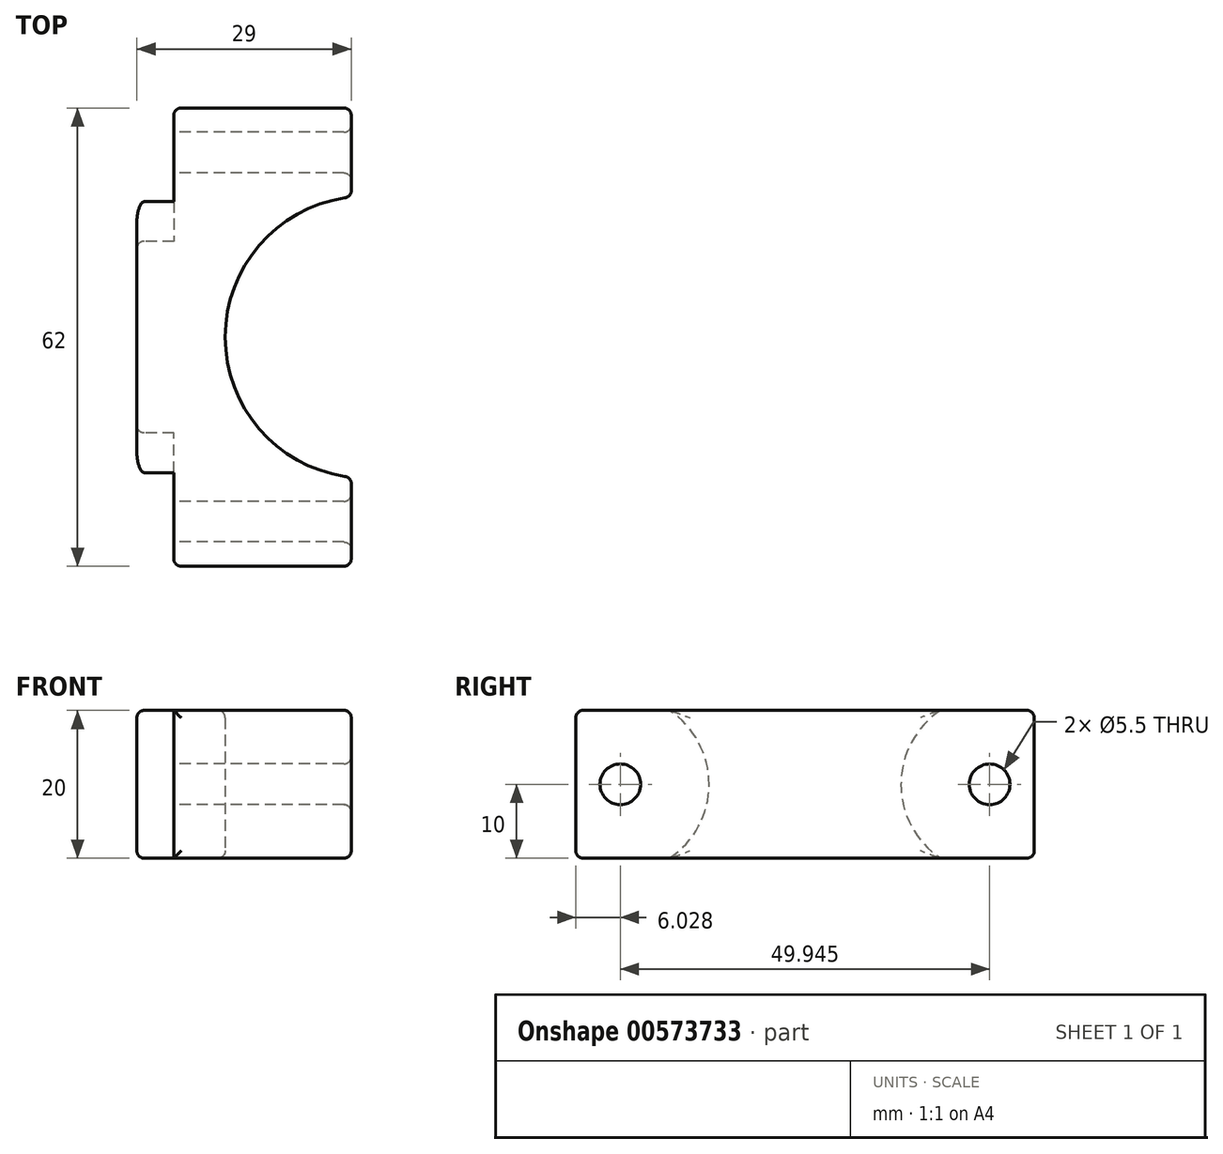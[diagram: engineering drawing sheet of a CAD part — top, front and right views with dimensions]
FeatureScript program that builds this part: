
annotation { "Feature Type Name" : "Feature", "Feature Type Description" : "" }
export const myFeature = defineFeature(function(context is Context, id is Id, definition is map)
    precondition{}
    {
        {
            var Q0;
            Q0=qCreatedBy(makeId("Top.planeOp"),FACE);
            var sketch = newSketch(context, id + "F0", { "sketchPlane" : qUnion([Q0])});
            skLineSegment(sketch, "E0.bottom", {"start": v(0, 0) * mm, "end": v(11.95, 0) * mm});
            skLineSegment(sketch, "E0.top", {"start": v(0, 31) * mm, "end": v(31, 31) * mm});
            skLineSegment(sketch, "E0.left", {"start": v(0, 0) * mm, "end": v(0, 31) * mm});
            skLineSegment(sketch, "E0.right", {"start": v(31, 19.05) * mm, "end": v(31, 31) * mm});
            skArc(sketch, "E1", {"start": v(31, 19.05) * mm, "mid": v(17.53, 13.47) * mm, "end": v(11.95, 0) * mm});
            skLineSegment(sketch, "E2.MirrorCS", {"start": v(0, 0) * mm, "end": v(0, -31) * mm});
            skLineSegment(sketch, "E3.MirrorCS", {"start": v(0, -31) * mm, "end": v(31, -31) * mm});
            skLineSegment(sketch, "E4.MirrorCS", {"start": v(31, -19.05) * mm, "end": v(31, -31) * mm});
            skArc(sketch, "E5.MirrorCS", {"start": v(31, -19.05) * mm, "mid": v(17.53, -13.47) * mm, "end": v(11.95, 0) * mm});
            skLineSegment(sketch, "E6", {"start": v(29, 31) * mm, "end": v(29, 18.94) * mm});
            skLineSegment(sketch, "E7.MirrorCS", {"start": v(29, -31) * mm, "end": v(29, -18.94) * mm});
            skSolve(sketch);
        }
        {
            var Q0;
            {var subQ0=sQuery(id+"F0.wireOp",EDGE,"E0.left");Q0=makeQuery(id+"F0.imprint","IMPRINT",FACE,{"disambiguationData":[TD([[makeQuery(id+"F0.imprint","IMPRINT",EDGE,{"derivedFrom":subQ0}),-1.0]])]});}
            var Q1;
            {var subQ4=sQuery(id+"F0.wireOp",EDGE,"E2.MirrorCS");Q1=makeQuery(id+"F0.imprint","IMPRINT",FACE,{"disambiguationData":[TD([[makeQuery(id+"F0.imprint","IMPRINT",EDGE,{"derivedFrom":subQ4}),1.0]])]});}
            extrude(context, id + "F1", {"entities" : qUnion([Q0, Q1]), "depth" : 20 * mm, "offsetDistance" : 25 * mm});
        }
        {
            var Q0;
            Q0=makeQuery(id+"F1.opExtrude","SWEPT_FACE",FACE,{"disambiguationData":[OSD([sQuery(id+"F0.wireOp",EDGE,"E0.left"),sQuery(id+"F0.wireOp",EDGE,"E2.MirrorCS")])]});
            var sketch = newSketch(context, id + "F2", { "sketchPlane" : qUnion([Q0])});
            skLineSegment(sketch, "E8.0.0", {"start": v(-18.94, 0) * mm, "end": v(-31, 0) * mm});
            skLineSegment(sketch, "E8.0.1", {"start": v(-31, 0) * mm, "end": v(-31, 20) * mm});
            skLineSegment(sketch, "E8.0.2", {"start": v(-31, 20) * mm, "end": v(-18.94, 20) * mm});
            skLineSegment(sketch, "E8.0.3", {"start": v(-18.94, 20) * mm, "end": v(-18.94, 0) * mm});
            skLineSegment(sketch, "E9", {"start": v(-24.97, 0) * mm, "end": v(-24.97, 20) * mm, "construction": true});
            skLineSegment(sketch, "E10", {"start": v(-31, 10) * mm, "end": v(-18.94, 10) * mm, "construction": true});
            skPoint(sketch, "E11", {"position": v(-24.97, 10) * mm});
            skPoint(sketch, "E12.MirrorP", {"position": v(24.97, 10) * mm});
            skSolve(sketch);
        }
        {
            var Q0;
            Q0=sQuery(id+"F2.wireOp",VERTEX,"E11");
            var Q1;
            Q1=sQuery(id+"F2.wireOp",VERTEX,"E12.MirrorP");
            var Q2;
            Q2=makeQuery(id+"F1.opExtrude","SWEPT_BODY",BODY,{"disambiguationData":[OSD([sQuery(id+"F0.wireOp",EDGE,"E0.top"),sQuery(id+"F0.wireOp",EDGE,"E0.left"),sQuery(id+"F0.wireOp",EDGE,"E0.right"),sQuery(id+"F0.wireOp",EDGE,"E1"),sQuery(id+"F0.wireOp",EDGE,"E2.MirrorCS"),sQuery(id+"F0.wireOp",EDGE,"E3.MirrorCS"),sQuery(id+"F0.wireOp",EDGE,"E4.MirrorCS"),sQuery(id+"F0.wireOp",EDGE,"E5.MirrorCS")])]});
            hole(context, id + "F3", {"style" : HoleStyle.C_BORE, "endStyle" : HoleEndStyle.THROUGH, "holeDiameter" : 5.5 * mm, "cBoreDiameter" : 24 * mm, "cBoreDepth" : 5 * mm, "isTappedThrough" : true, "tappedDepth" : 12 * mm, "tapClearance" : 3, "locations" : qUnion([Q0, Q1]), "scope" : qUnion([Q2]), "majorDiameter" : 5 * mm});
        }
        {
            var Q0;
            Q0=makeQuery(id+"F1.opExtrude","SWEPT_FACE",FACE,{"disambiguationData":[OSD([sQuery(id+"F0.wireOp",EDGE,"E0.left"),sQuery(id+"F0.wireOp",EDGE,"E2.MirrorCS")])]});
            var Q1;
            Q1=makeQuery(id+"F1.opExtrude","SWEPT_FACE",FACE,{"disambiguationData":[OSD([sQuery(id+"F0.wireOp",EDGE,"E0.top")])]});
            var Q2;
            Q2=makeQuery(id+"F1.opExtrude","SWEPT_FACE",FACE,{"disambiguationData":[OSD([sQuery(id+"F0.wireOp",EDGE,"E3.MirrorCS")])]});
            var Q3;
            Q3=makeQuery(id+"F1.opExtrude","SWEPT_FACE",FACE,{"disambiguationData":[OSD([sQuery(id+"F0.wireOp",EDGE,"E1"),sQuery(id+"F0.wireOp",EDGE,"E5.MirrorCS")])]});
            var Q4;
            Q4=makeQuery(id+"F1.opExtrude","SWEPT_FACE",FACE,{"disambiguationData":[OSD([sQuery(id+"F0.wireOp",EDGE,"E6")])]});
            var Q5;
            Q5=makeQuery(id+"F1.opExtrude","SWEPT_FACE",FACE,{"disambiguationData":[OSD([sQuery(id+"F0.wireOp",EDGE,"E7.MirrorCS")])]});
            fillet(context, id + "F4", {"entities" : qUnion([Q0, Q1, Q2, Q3, Q4, Q5]), "radius" : 1 * mm, "tangentPropagation" : true, "allowEdgeOverflow" : false});
        }
    });
